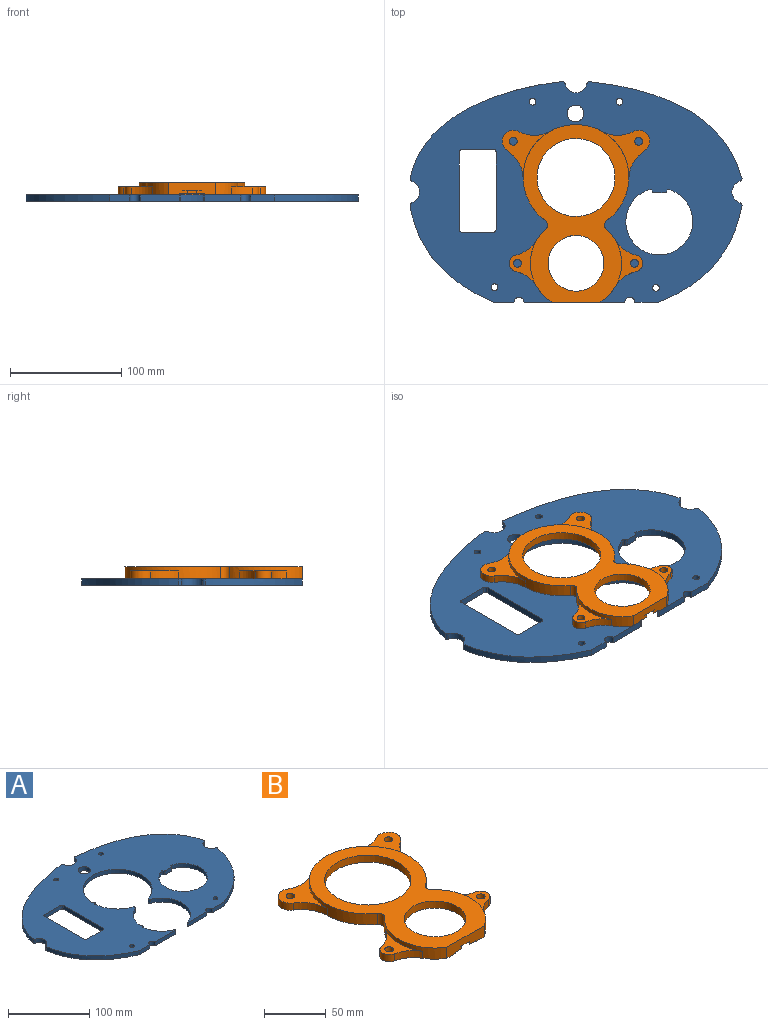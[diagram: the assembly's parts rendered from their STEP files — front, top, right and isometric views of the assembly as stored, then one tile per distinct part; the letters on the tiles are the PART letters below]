
ASSEMBLY  parts=2 mates=1
PART A: 56 faces, bbox 298x198x6 mm
  f0: cylinder r=35.5mm len=30.92mm, axis (0,0,-1), area 240.8mm2, adj f1,f50,f54,f55
  f1: cylinder r=2mm len=6mm, axis (0,0,-1), area 29.2mm2, adj f0,f2,f54,f55
  f2: cylinder r=42.5mm len=37.83mm, axis (0,0,-1), area 303.7mm2, adj f1,f3,f54,f55
  f3: cylinder r=2.5mm len=6mm, axis (0,0,-1), area 46.2mm2, adj f2,f4,f54,f55
  f4: cylinder r=42.5mm len=84.93mm, axis (0,0,-1), area 1104.8mm2, adj f3,f5,f54,f55
  f5: cylinder r=2mm len=6mm, axis (0,0,-1), area 29.2mm2, adj f4,f6,f54,f55
  f6: cylinder r=35.5mm len=66.61mm, axis (0,0,-1), area 519.2mm2, adj f5,f7,f54,f55
  f7: cylinder r=1mm len=6mm, axis (0,0,-1), area 5.5mm2, adj f6,f8,f54,f55
  f8: cylinder r=1mm len=6mm, axis (0,0,-1), area 7.5mm2, adj f7,f9,f54,f55
  f9: plane 32.3x6mm, normal (0,-1,0), area 193.8mm2, adj f8,f10,f54,f55
  f10: cylinder r=4.5mm len=9mm, axis (0,0,-1), area 84.8mm2, adj f9,f11,f54,f55
  f11: plane 21.2x6mm, normal (0,-1,0), area 127.2mm2, adj f10,f12,f54,f55
  f12: extruded ~87.17x75mm, area 724.9mm2, adj f11,f13,f54,f55
  f13: cylinder r=2.55mm len=6mm, axis (0,0,-1), area 17.5mm2, adj f12,f14,f54,f55
  f14: cylinder r=10mm len=19.28mm, axis (0,0,-1), area 156.1mm2, adj f13,f15,f54,f55
  f15: cylinder r=2.55mm len=6mm, axis (0,0,-1), area 17.5mm2, adj f14,f16,f54,f55
  f16: extruded ~137.17x87.17mm, area 1041.5mm2, adj f15,f17,f54,f55
  f17: cylinder r=2mm len=6mm, axis (0,0,-1), area 16.8mm2, adj f16,f18,f54,f55
  f18: cylinder r=10mm len=19.72mm, axis (0,0,-1), area 168.4mm2, adj f17,f19,f54,f55
  f19: cylinder r=2mm len=6mm, axis (0,0,-1), area 16.8mm2, adj f18,f20,f54,f55
  f20: plane 6x1.36mm, normal (0,1,0), area 8.2mm2, adj f19,f21,f54,f55
  f21: extruded ~135.81x87.17mm, area 1033.7mm2, adj f20,f22,f54,f55
  f22: cylinder r=3.04mm len=6mm, axis (0,0,-1), area 18mm2, adj f21,f23,f54,f55
  f23: cylinder r=10mm len=18.97mm, axis (0,0,-1), area 149.8mm2, adj f22,f24,f54,f55
  f24: cylinder r=3.04mm len=6mm, axis (0,0,-1), area 18mm2, adj f23,f25,f54,f55
  f25: extruded ~87.17x75mm, area 723.1mm2, adj f24,f26,f54,f55
  f26: plane 18.33x6mm, normal (0,-1,0), area 110mm2, adj f25,f27,f54,f55
  f27: cylinder r=4.5mm len=9mm, axis (0,0,-1), area 84.8mm2, adj f26,f28,f54,f55
  f28: plane 35.17x6mm, normal (0,-1,0), area 211mm2, adj f27,f29,f54,f55
  f29: cylinder r=1mm len=6mm, axis (0,0,-1), area 7.5mm2, adj f28,f30,f54,f55
  f30: cylinder r=1mm len=6mm, axis (0,0,-1), area 5.5mm2, adj f29,f31,f54,f55
  f31: cylinder r=35.5mm len=31.69mm, axis (0,0,-1), area 254.3mm2, adj f30,f50,f54,f55
  f32: plane 10.76x6mm, normal (0,-1,0), area 64.5mm2, adj f33,f51,f54,f55
  f33: cylinder r=1mm len=6mm, axis (0,0,-1), area 6.7mm2, adj f32,f34,f54,f55
  f34: plane 6x1.75mm, normal (0.9,-0.44,0), area 11.7mm2, adj f33,f35,f54,f55
  f35: cylinder r=1mm len=6mm, axis (0,0,-1), area 8.4mm2, adj f34,f36,f54,f55
  f36: cylinder r=30mm len=60mm, axis (0,0,-1), area 1029.9mm2, adj f35,f37,f54,f55
  f37: cylinder r=1mm len=6mm, axis (0,0,-1), area 8.4mm2, adj f36,f38,f54,f55
  f38: plane 6x1.75mm, normal (-0.9,-0.44,0), area 11.7mm2, adj f37,f51,f54,f55
  f39: plane 29x6mm, normal (0,1,0), area 174mm2, adj f40,f52,f54,f55
  f40: cylinder r=2mm len=6mm, axis (0,0,-1), area 18.8mm2, adj f39,f41,f54,f55
  f41: plane 70x6mm, normal (1,0,0), area 420mm2, adj f40,f42,f54,f55
  f42: cylinder r=2mm len=6mm, axis (0,0,-1), area 18.8mm2, adj f41,f43,f54,f55
  f43: plane 29x6mm, normal (0,-1,0), area 174mm2, adj f42,f44,f54,f55
  f44: cylinder r=2mm len=6mm, axis (0,0,-1), area 18.8mm2, adj f43,f45,f54,f55
  f45: plane 70x6mm, normal (-1,0,0), area 420mm2, adj f44,f52,f54,f55
  f46: cylinder r=7.5mm len=15mm, axis (0,0,-1), area 282.7mm2, adj f54,f55
  f47: cylinder r=3mm len=6mm, axis (0,0,-1), area 113.1mm2, adj f54,f55
  f48: cylinder r=3mm len=6mm, axis (0,0,-1), area 113.1mm2, adj f54,f55
  f49: cylinder r=3mm len=6mm, axis (0,0,-1), area 113.1mm2, adj f54,f55
  f50: cylinder r=2mm len=6mm, axis (0,0,-1), area 37mm2, adj f0,f31,f54,f55
  f51: cylinder r=1mm len=6mm, axis (0,0,-1), area 6.7mm2, adj f32,f38,f54,f55
  f52: cylinder r=2mm len=6mm, axis (0,0,-1), area 18.8mm2, adj f39,f45,f54,f55
  f53: cylinder r=3mm len=6mm, axis (0,0,-1), area 113.1mm2, adj f54,f55
  f54: plane 298x198mm, normal (0,0,1), area 32992mm2, adj f0,f1,f2,f3,f4,f5,f6,f7
  f55: plane 298x198mm, normal (0,0,-1), area 32992mm2, adj f0,f1,f2,f3,f4,f5,f6,f7
PART B: 52 faces, bbox 132.6x159.5x11 mm
  f0: cylinder r=10mm len=18.48mm, axis (0,0,-1), area 215mm2, adj f3,f4,f14,f30
  f1: cylinder r=10mm len=18.48mm, axis (0,0,-1), area 215mm2, adj f2,f5,f13,f30
  f2: cylinder r=30mm len=24.89mm, axis (0,0,1), area 208.7mm2, adj f1,f6,f13,f30
  f3: cylinder r=30mm len=24.89mm, axis (0,0,1), area 208.7mm2, adj f0,f6,f14,f30
  f4: cylinder r=30mm len=28.61mm, axis (0,0,1), area 208.7mm2, adj f0,f6,f14,f30
  f5: cylinder r=30mm len=28.61mm, axis (0,0,1), area 208.7mm2, adj f1,f6,f13,f30
  f6: cylinder r=47.5mm len=95mm, axis (0,0,-1), area 1911.8mm2, adj f2,f3,f4,f5,f13,f14,f30,f41
  f7: cylinder r=42.25mm len=84.5mm, axis (0,0,1), area 775mm2, adj f8,f9,f12,f19,f30,f40,f46,f47
  f8: cylinder r=35.25mm len=69.98mm, axis (0,0,1), area 306.5mm2, adj f7,f25,f40,f47
  f9: cylinder r=2.5mm len=1mm, axis (0,0,-1), area 0.3mm2, adj f7,f12,f18,f30
  f10: cylinder r=2mm len=1mm, axis (0,0,-1), area 0.3mm2, adj f11,f28,f30,f46
  f11: plane 33.02x31.25mm, normal (0,0,-1), area 14.7mm2, adj f10,f25,f26,f27,f28,f46
  f12: plane 72.54x38.05mm, normal (0,0,-1), area 34.8mm2, adj f7,f9,f16,f17,f18,f29,f46
  f13: plane 43.37x43.3mm, normal (0,0,1), area 596.2mm2, adj f1,f2,f5,f6,f37
  f14: plane 43.37x43.3mm, normal (0,0,1), area 596.2mm2, adj f0,f3,f4,f6,f36
  f15: plane 42.22x24.85mm, normal (0,0,1), area 322.7mm2, adj f31,f32,f35,f44,f45
  f16: cylinder r=35.5mm len=30.92mm, axis (0,0,-1), area 40.1mm2, adj f12,f17,f29,f30
  f17: cylinder r=2mm len=3.75mm, axis (0,0,-1), area 4.9mm2, adj f12,f16,f18,f30
  f18: cylinder r=42.5mm len=37.83mm, axis (0,0,-1), area 50.6mm2, adj f9,f12,f17,f30
  f19: cylinder r=2.5mm len=1mm, axis (0,0,-1), area 0.3mm2, adj f7,f20,f30,f40
  f20: cylinder r=42.5mm len=84.93mm, axis (0,0,-1), area 184.1mm2, adj f19,f21,f30,f40
  f21: cylinder r=2mm len=3.75mm, axis (0,0,-1), area 4.9mm2, adj f20,f22,f30,f40
  f22: cylinder r=35.5mm len=66.61mm, axis (0,0,-1), area 86.5mm2, adj f21,f23,f30,f40
  f23: cylinder r=1mm len=1mm, axis (0,0,-1), area 0.9mm2, adj f22,f24,f30,f40
  f24: cylinder r=1mm len=1mm, axis (0,0,-1), area 1.2mm2, adj f23,f25,f30,f40
  f25: plane 42.71x11mm, normal (0,-1,0), area 421.6mm2, adj f8,f11,f24,f26,f30,f31,f33,f40
  f26: cylinder r=1mm len=1mm, axis (0,0,-1), area 1.2mm2, adj f11,f25,f27,f30
  f27: cylinder r=1mm len=1mm, axis (0,0,-1), area 0.9mm2, adj f11,f26,f28,f30
  f28: cylinder r=35.5mm len=31.69mm, axis (0,0,-1), area 42.4mm2, adj f10,f11,f27,f30
  f29: cylinder r=2mm len=1mm, axis (0,0,-1), area 0.3mm2, adj f12,f16,f30,f46
  f30: plane 159.5x132.58mm, normal (0,0,-1), area 4077mm2, adj f0,f1,f2,f3,f4,f5,f6,f7
  f31: cylinder r=41mm len=65.61mm, axis (0,0,-1), area 531.1mm2, adj f15,f25,f30,f41,f44,f45,f50
  f32: cylinder r=7.5mm len=14.62mm, axis (0,0,-1), area 141.3mm2, adj f15,f30,f44,f45
  f33: cylinder r=41mm len=65.61mm, axis (0,0,-1), area 531.1mm2, adj f25,f30,f39,f41,f42,f43,f51
  f34: cylinder r=7.5mm len=14.62mm, axis (0,0,-1), area 141.3mm2, adj f30,f39,f42,f43
  f35: cylinder r=3.5mm len=7mm, axis (0,0,-1), area 153.9mm2, adj f15,f30
  f36: cylinder r=3.5mm len=7mm, axis (0,0,-1), area 153.9mm2, adj f14,f30
  f37: cylinder r=3.5mm len=7mm, axis (0,0,-1), area 153.9mm2, adj f13,f30
  f38: cylinder r=3.5mm len=7mm, axis (0,0,-1), area 153.9mm2, adj f30,f39
  f39: plane 42.22x24.85mm, normal (0,0,1), area 322.7mm2, adj f33,f34,f38,f42,f43
  f40: plane 154.5x84.93mm, normal (0,0,-1), area 83.8mm2, adj f7,f8,f19,f20,f21,f22,f23,f24
  f41: plane 159.5x95mm, normal (0,0,1), area 6067.8mm2, adj f6,f25,f31,f33,f48,f49,f50,f51
  f42: cylinder r=30mm len=19.02mm, axis (0,0,1), area 169mm2, adj f30,f33,f34,f39
  f43: cylinder r=30mm len=19.03mm, axis (0,0,1), area 169mm2, adj f30,f33,f34,f39
  f44: cylinder r=30mm len=19.03mm, axis (0,0,1), area 169mm2, adj f15,f30,f31,f32
  f45: cylinder r=30mm len=19.02mm, axis (0,0,1), area 169mm2, adj f15,f30,f31,f32
  f46: cylinder r=35.25mm len=69.98mm, axis (0,0,1), area 310.4mm2, adj f7,f10,f11,f12,f25,f29,f30,f47
  f47: plane 154.25x84.5mm, normal (0,0,-1), area 3695.3mm2, adj f7,f8,f25,f46,f48,f49
  f48: cylinder r=35mm len=70mm, axis (0,0,1), area 1539.4mm2, adj f41,f47
  f49: cylinder r=25mm len=50mm, axis (0,0,1), area 1099.6mm2, adj f41,f47
  f50: cylinder r=5mm len=11mm, axis (0,0,1), area 98.5mm2, adj f6,f30,f31,f41
  f51: cylinder r=5mm len=11mm, axis (0,0,1), area 98.5mm2, adj f6,f30,f33,f41
PLACE A t=(-0.62,-2.77,-6.62)mm
PLACE B t=(-0.62,-2.77,-0.62)mm
MATE cylindrical B.f6 <-> A.f4  axis (0,0,-1) through (-0.62,10.23,-0.62)mm
